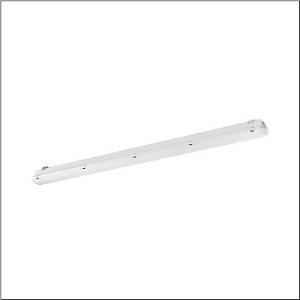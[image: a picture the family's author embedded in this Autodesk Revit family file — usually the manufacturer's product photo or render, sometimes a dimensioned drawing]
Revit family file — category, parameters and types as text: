
# Revit family: monsun_r__11xtreme_mo_51fe107p440j005_dc0f
name_source: partatom
category: Lighting Fixtures
units: mm (PartAtom-declared; Revit-internal decimal feet)

## family parameters
Cut with Voids When Loaded = No
Host = Face
Light Source = No
Part Type = Normal
Room Calculation Point = No
Round Connector Dimension = Use Diameter
Shared = No

## types (1)
- Monsun® 11Xtreme MO (1 x LED, 4200 lm, 23.3 W, 4000K)
    Apparent Load = 23 VA
    CIE Flux Codes = 47 77 93 94 100
    Color Rendering = 80
    Color Temperature = 4000K
    Default Elevation = 1800 mm
    Description = Monsun® 11Xtreme MO, damp-proof luminaire, chain hanger, primary optical cover: enclosure, of PMMA, light emission: direct distribution, primary light characteristic: symmetric, installation type: suspended mounting, surface-mounted, horizontal mounting, vertical mounting, LED, rated luminous flux: 4.200lm, luminous efficacy: 174lm/W, light colour: 840, colour temperature: 4000K, control gear: ON/OFF, with terminal, 3-pole, max. 2.5mm², through-wiring: 5x 2.5mm², mains connection: 220..240V, AC, 50/60Hz, rated input power: 24W, luminaire housing, of glass-fibre reinforced polyester, uncoated, bright grey, incl. chain hanger, length: 1.590mm, width: 90mm, height: 88mm, clip for enclosure, of stainless steel (V2A), ceiling mounting element, of stainless steel (V2A), chain hanger, of stainless steel (V2A), protection rating (complete): IP66, insulation class (complete): insulation class I (protective earthing), certification: CE, ENEC, VDE, UKCA, protection symbol: D, impact resistance: IK04, permissible operating ambient temperature: -35..+55°C, standard: EN 60598-2-1, EN 50419, corresponds to IFS (International Featured Standards) requirements for safety and quality in the food industry, for indoor or canopied outdoor use, no direct snow, no direct sun, no direct rain, contact your sales advisor before using the luminaires in applications with unclear chemical exposure, large temperature fluctuations or condensation-forming humidity, LABS conformity tested according to VDMA 24364:2018-05, packaging unit: 1 piece
    Height = 88 mm
    Lamp = 1 x LED
    Lamp Light Flux = 4200 lm
    Lamp Power = 23.3 W
    Lamp count = 1
    Length = 1590 mm
    Luminous efficacy = 180 lm/W
    Manufacturer = Siteco
    ModVariant = No
    Model = 51FE107P440J005
    Mounting Place = Ceiling
    Mounting Type = Surface mounted
    Number of Poles = 1
    OnlyDefault = Yes
    Power Factor = 1
    Product Name = Monsun® 11Xtreme MO
    Product group = damp-proof luminaire
    ProductGroupID = 300
    Protection Class = Protection class I
    Protection Degree = IP 66
    RLX_Detail_Level = 1
    RLX_Emergency_Light_Flux = 0 lm
    RLX_Emergency_Type = 0
    RLX_Emergency_Type_DB = No
    RlxData = <blob elided: 12449 chars, md5=e1674b44>
    Socket = socket
    Standby Power = 0 W
    System Light Flux = 4200 lm
    System Power = 23 W
    Type Comments = Product without accessories
    Type Image = l_1349234.jpg
    URL = http://relux.com
    VarID = ---
    Voltage = 0 V
    Weight = 0.00 kg
    Width = 90 mm

## geometry (parser evidence)
native form markers: Sweep x13
no freeform markers — native parametric forms only
